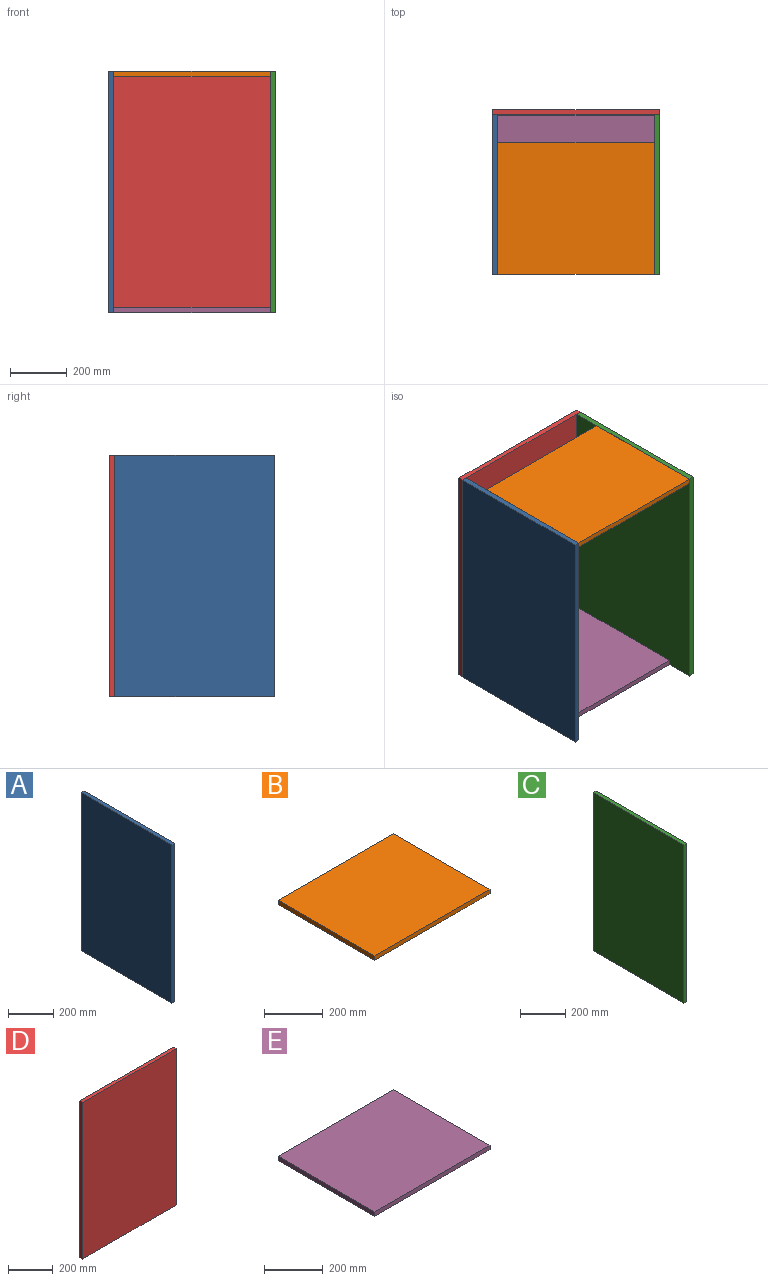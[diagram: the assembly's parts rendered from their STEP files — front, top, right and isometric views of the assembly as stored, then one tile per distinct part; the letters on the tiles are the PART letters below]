
ASSEMBLY  parts=5 mates=4
PART A: 6 faces, bbox 18x564x853 mm
  f0: plane 853x564mm, normal (1,0,0), area 481092mm2, adj f1,f3,f4,f5
  f1: plane 564x18mm, normal (0,0,1), area 10152mm2, adj f0,f2,f4,f5
  f2: plane 853x564mm, normal (-1,0,0), area 481092mm2, adj f1,f3,f4,f5
  f3: plane 564x18mm, normal (0,0,-1), area 10152mm2, adj f0,f2,f4,f5
  f4: plane 853x18mm, normal (0,-1,0), area 15354mm2, adj f0,f1,f2,f3
  f5: plane 853x18mm, normal (0,1,0), area 15354mm2, adj f0,f1,f2,f3
PART B: 6 faces, bbox 554x464x18 mm
  f0: plane 554x18mm, normal (0,1,0), area 9972mm2, adj f2,f3,f4,f5
  f1: plane 554x18mm, normal (0,-1,0), area 9972mm2, adj f2,f3,f4,f5
  f2: plane 464x18mm, normal (-1,0,0), area 8352mm2, adj f0,f1,f3,f4
  f3: plane 554x464mm, normal (0,0,-1), area 257056mm2, adj f0,f1,f2,f5
  f4: plane 554x464mm, normal (0,0,1), area 257056mm2, adj f0,f1,f2,f5
  f5: plane 464x18mm, normal (1,0,0), area 8352mm2, adj f0,f1,f3,f4
PART C: 6 faces, bbox 18x564x853 mm
  f0: plane 853x564mm, normal (1,0,0), area 481092mm2, adj f1,f3,f4,f5
  f1: plane 564x18mm, normal (0,0,1), area 10152mm2, adj f0,f2,f4,f5
  f2: plane 853x564mm, normal (-1,0,0), area 481092mm2, adj f1,f3,f4,f5
  f3: plane 564x18mm, normal (0,0,-1), area 10152mm2, adj f0,f2,f4,f5
  f4: plane 853x18mm, normal (0,-1,0), area 15354mm2, adj f0,f1,f2,f3
  f5: plane 853x18mm, normal (0,1,0), area 15354mm2, adj f0,f1,f2,f3
PART D: 6 faces, bbox 590x18x853 mm
  f0: plane 853x590mm, normal (0,-1,0), area 503270mm2, adj f1,f2,f3,f4
  f1: plane 590x18mm, normal (0,0,-1), area 10620mm2, adj f0,f2,f4,f5
  f2: plane 853x18mm, normal (1,0,0), area 15354mm2, adj f0,f1,f3,f5
  f3: plane 590x18mm, normal (0,0,1), area 10620mm2, adj f0,f2,f4,f5
  f4: plane 853x18mm, normal (-1,0,0), area 15354mm2, adj f0,f1,f3,f5
  f5: plane 853x590mm, normal (0,1,0), area 503270mm2, adj f1,f2,f3,f4
PART E: 6 faces, bbox 554x464x18 mm
  f0: plane 554x18mm, normal (0,-1,0), area 9972mm2, adj f1,f3,f4,f5
  f1: plane 464x18mm, normal (-1,0,0), area 8352mm2, adj f0,f2,f3,f4
  f2: plane 554x18mm, normal (0,1,0), area 9972mm2, adj f1,f3,f4,f5
  f3: plane 554x464mm, normal (0,0,-1), area 257056mm2, adj f0,f1,f2,f5
  f4: plane 554x464mm, normal (0,0,1), area 257056mm2, adj f0,f1,f2,f5
  f5: plane 464x18mm, normal (1,0,0), area 8352mm2, adj f0,f2,f3,f4
PLACE A at identity
PLACE B at identity
PLACE C at identity
PLACE D at identity
PLACE E at identity
MATE fastened C.f3 <-> D.f1  axis (0,0,-1) through (1038,-436,120)mm
MATE fastened C.f1 <-> B.f4  axis (0,0,1) through (1020,-1000,973)mm
MATE fastened A.f1 <-> B.f4  axis (0,0,1) through (466,-1000,973)mm
MATE fastened E.f2 <-> C.f5  axis (0,1,0) through (1020,-436,120)mm
